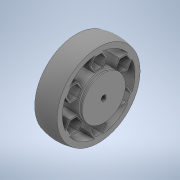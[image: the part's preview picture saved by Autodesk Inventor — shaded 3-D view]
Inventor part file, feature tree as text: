
AUTODESK INVENTOR PART (.ipt)
format: ipt  version: 2020 (Build 240168000, 168)  size: 302,080 bytes
history: native  units: in
note: dims shown in document units (in); Inventor stores cm internally (conversion verified against a paired STEP export)
features: sketch x4, extrude x2, revolve x2, projected_geometry x1
ambient origin geometry x8: Origin, YZ Plane, XZ Plane, XY Plane, X Axis, Y Axis, Z Axis, Center Point
bodies: Solid1 (feature_tree)
feature tree (9):
  extrude  "Extrusion1"  Depth=0.1181in
  sketch  "Sketch3"  dims[d6=0.9843in d7=0.1181in]
  revolve  "Revolution1"  [1 undecoded]
  extrude  "Extrusion2"  Depth=0.1181in
  revolve  "Revolution2"  [1 undecoded]
  sketch  "Sketch1"  dims[d0=0.1181in d1=0.0394in]
  sketch  "Sketch2"  dims[d3=1.8898in d4=0.1181in]
  projected_geometry  "Projected Loop1"
  sketch  "Sketch4"  dims[d8=0.0in d9=1.8898in d10=0.1181in d11=0.0315in d12=2.3622in d14=360.0deg d16=0.5118in d17=0.0in d19=90.0deg d20=0.0394in d22=60.0deg d24=0.0394in d25=90.0deg d26=60.0deg]
note: 2 required parameter values undecoded (feature->parameter linkage not recoverable at this tier; creation-order binding heuristic only, values carry confidence <= 0.55)
